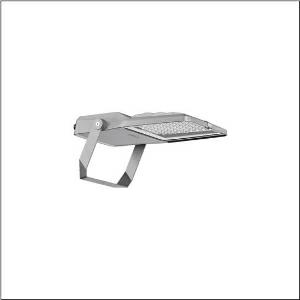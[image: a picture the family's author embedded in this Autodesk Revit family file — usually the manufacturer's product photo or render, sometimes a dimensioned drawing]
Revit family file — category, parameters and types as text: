
# Revit family: floodlight_fl_21_mini___pl43_5xa7772c2a1a_c35c
name_source: partatom
category: Lighting Fixtures
units: mm (PartAtom-declared; Revit-internal decimal feet)

## family parameters
Cut with Voids When Loaded = No
Host = Face
Light Source = No
Part Type = Normal
Room Calculation Point = No
Round Connector Dimension = Use Diameter
Shared = No

## types (1)
- --- (1 x LED, 12520 lm, 87.2 W, 3000K)
    Apparent Load = 87 VA
    CIE Flux Codes = 27 78 99 100 100
    Color Rendering = 70
    Color Temperature = 3000K
    Default Elevation = 1800 mm
    Description = Floodlight FL 21 mini, floodlight, primary light control with lens, of PMMA, primary optical cover: protective disc, of toughened safety glass, transparent, light distribution: PL43, light emission: direct distribution, installation type: surface-mounted, LED, High Power LED, rated luminous flux: 12.520lm, luminous efficacy: 144lm/W, light colour: 730, colour temperature: 3000K, control gear: ECG iQ, control: Street-Remote, Auto-Match, Temp-Guard, Night-Set, Smart-Wire, Desk-Remote (wireless, voltage-free reading and setting of iQ features in the workshop via application-optimized NFC function/RFID function), optimised constant luminous flux control (CLO 2.0), with terminal, 6-pole, mains connection: 220..240V, AC, 50/60Hz, start of lifetime: 87W, end of lifetime: 92W, reduction: 40W, luminaire housing, of diecast aluminium, powder-coated, Siteco® metallic grey (DB 702S), corrosivity category C5 according to DIN EN ISO 12944, mounting bracket, of steel, galvanised, powder-coated, Siteco® metallic grey (DB 702S), protection rating (complete): IP66, insulation class (complete): insulation class II (safety insulation), certification: CE, ENEC, VDE, protection symbol: D, impact resistance: IK08, permissible operating ambient temperature: -40..+40°C, permissible operating ambient temperature for outdoor applications: -40..+50°C, standard: DIN EN 12944, packaging unit: 1 piece

Light Distribution: PL43
    Height = 70 mm
    Lamp = 1 x LED
    Lamp Light Flux = 12520 lm
    Lamp Power = 87.2 W
    Lamp count = 1
    Length = 485 mm
    Luminous efficacy = 144 lm/W
    Manufacturer = Siteco
    ModVariant = No
    Model = 5XA7772C2A1A
    Number of Poles = 1
    OnlyDefault = Yes
    Power Factor = 1
    Product Name = Floodlight FL 21 mini | PL43
    Product group = floodlight | pylon top
    ProductGroupID = 6101
    Protection Class = Protection class II
    Protection Degree = IP 66
    RLX_Detail_Level = 1
    RlxData = <blob elided: 95921 chars, md5=3a94528a>
    Socket = socket
    Standby Power = 0 W
    System Light Flux = 12520 lm
    System Power = 87 W
    Type Comments = factory setting: luminous flux: 100 % | dim-lin: 254 | 456 mA
    Type Image = l_1006845.jpg
    URL = http://relux.com
    VarID = @adj_073761
    Voltage = 0 V
    Weight = 0.00 kg
    Width = 337 mm

## geometry (parser evidence)
native form markers: Blend x4, Sweep x14
no freeform markers — native parametric forms only
